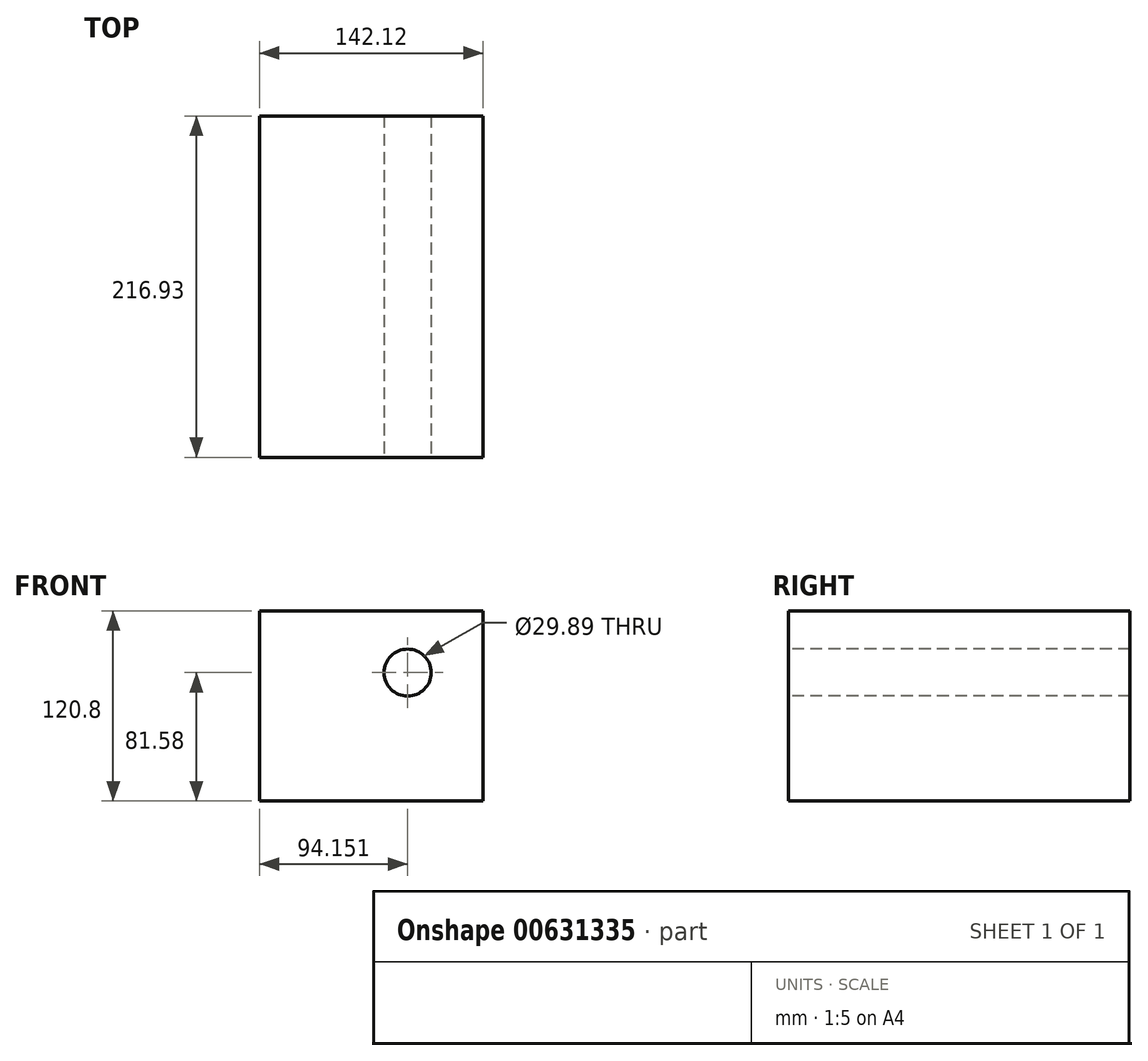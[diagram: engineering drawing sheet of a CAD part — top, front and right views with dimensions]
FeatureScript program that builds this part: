
annotation { "Feature Type Name" : "Feature", "Feature Type Description" : "" }
export const myFeature = defineFeature(function(context is Context, id is Id, definition is map)
    precondition{}
    {
        {
            var Q0;
            Q0=qCreatedBy(makeId("Front.planeOp"),FACE);
            var sketch = newSketch(context, id + "F0", { "sketchPlane" : qUnion([Q0])});
            skLineSegment(sketch, "E0.bottom", {"start": v(-25.52, -22.63) * mm, "end": v(116.6, -22.63) * mm});
            skLineSegment(sketch, "E0.top", {"start": v(-25.52, 98.17) * mm, "end": v(116.6, 98.17) * mm});
            skLineSegment(sketch, "E0.left", {"start": v(-25.52, -22.63) * mm, "end": v(-25.52, 98.17) * mm});
            skLineSegment(sketch, "E0.right", {"start": v(116.6, -22.63) * mm, "end": v(116.6, 98.17) * mm});
            skPoint(sketch, "E0.middle", {"position": v(45.54, 37.77) * mm});
            skSolve(sketch);
        }
        {
            var Q0;
            Q0=makeQuery(id+"F0.imprint","IMPRINT",FACE,{"disambiguationData":[TD([[makeQuery(id+"F0.imprint","IMPRINT",EDGE,{"derivedFrom":sQuery(id+"F0.wireOp",EDGE,"E0.bottom")}),1.0]])]});
            var Q1;
            Q1=sQuery(id+"F0.wireOp",EDGE,"E0.right");
            extrude(context, id + "F1", {"entities" : qUnion([Q0]), "surfaceEntities" : qUnion([Q1]), "depth" : 127 * mm, "offsetDistance" : 25.4 * mm});
        }
        {
            var Q0;
            Q0=makeQuery(id+"F1.opExtrude","CAP_FACE",FACE,{"disambiguationData":[OSD([sQuery(id+"F0.wireOp",EDGE,"E0.bottom"),sQuery(id+"F0.wireOp",EDGE,"E0.top"),sQuery(id+"F0.wireOp",EDGE,"E0.left"),sQuery(id+"F0.wireOp",EDGE,"E0.right")])],"isStart":false});
            var sketch = newSketch(context, id + "F2", { "sketchPlane" : qUnion([Q0])});
            skCircle(sketch, "E1", {"center": v(68.63, 58.95) * mm, "radius": 14.94 * mm});
            skSolve(sketch);
        }
        {
            var Q0;
            Q0=makeQuery(id+"F2.imprint","IMPRINT",FACE,{"disambiguationData":[TD([[makeQuery(id+"F2.imprint","IMPRINT",EDGE,{"derivedFrom":sQuery(id+"F2.wireOp",EDGE,"E1")}),1.0]])]});
            var Q1;
            Q1=sQuery(id+"F2.wireOp",EDGE,"E1");
            extrude(context, id + "F3", {"entities" : qUnion([Q0]), "operationType" : NewBodyOperationType.REMOVE, "surfaceEntities" : qUnion([Q1]), "endBound" : BoundingType.THROUGH_ALL, "oppositeDirection" : true, "depth" : 25.4 * mm, "offsetDistance" : 25.4 * mm});
        }
        {
            var Q0;
            Q0=makeQuery(id+"F1.opExtrude","CAP_FACE",FACE,{"disambiguationData":[OSD([sQuery(id+"F0.wireOp",EDGE,"E0.bottom"),sQuery(id+"F0.wireOp",EDGE,"E0.top"),sQuery(id+"F0.wireOp",EDGE,"E0.left"),sQuery(id+"F0.wireOp",EDGE,"E0.right")])],"isStart":false});
            var sketch = newSketch(context, id + "F4", { "sketchPlane" : qUnion([Q0])});
            skCircle(sketch, "E2", {"center": v(0, 19.76) * mm, "radius": 26.24 * mm});
            skSolve(sketch);
        }
        {
            var Q0;
            {var subQ1=makeQuery(id+"F1.opExtrude","CAP_EDGE",EDGE,{"disambiguationData":[OSD([sQuery(id+"F0.wireOp",EDGE,"E0.bottom")])],"isStart":false});Q0=makeQuery(id+"F4.imprint","IMPRINT",FACE,{"disambiguationData":[TD([[makeQuery(id+"F4.imprint","IMPRINT",EDGE,{"derivedFrom":subQ1}),1.0]])]});}
            var Q1;
            {var subQ0=sQuery(id+"F4.wireOp",EDGE,"E2");var subQ1=makeQuery(id+"F1.opExtrude","CAP_EDGE",EDGE,{"disambiguationData":[OSD([sQuery(id+"F0.wireOp",EDGE,"E0.left")])],"isStart":false});var subQ2=makeQuery(id+"F4.imprint","INTERSECT",VERTEX,{"disambiguationData":[OD(0.0)],"derivedFrom":[subQ1,subQ0]});Q1=makeQuery(id+"F4.imprint","IMPRINT",FACE,{"disambiguationData":[TD([[makeQuery(id+"F4.imprint","IMPRINT",EDGE,{"disambiguationData":[TD([[subQ2,-1.0]])],"derivedFrom":subQ0}),1.0]])]});}
            extrude(context, id + "F5", {"entities" : qUnion([Q0, Q1]), "operationType" : NewBodyOperationType.ADD, "depth" : 89.93 * mm, "offsetDistance" : 25.4 * mm});
        }
    });
